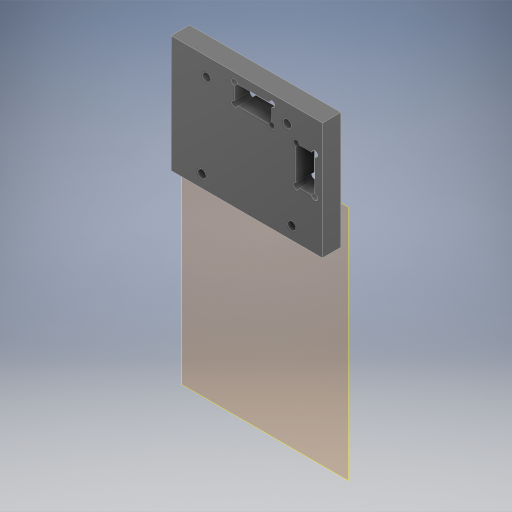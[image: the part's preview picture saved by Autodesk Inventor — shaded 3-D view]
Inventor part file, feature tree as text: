
AUTODESK INVENTOR PART (.ipt)
format: ipt  version: 2024 (Build 280153000, 153)  size: 323,072 bytes
history: native  units: in
note: dims shown in document units (in); Inventor stores cm internally (conversion verified against a paired STEP export)
features: other x3, extrude x3, sketch x3, reference x1
ambient origin geometry x8: Origin, YZ Plane, XZ Plane, XY Plane, X Axis, Y Axis, Z Axis, Center Point
bodies: Body1 (feature_tree)
feature tree (10):
  other  "작업 평면1"
  extrude  "돌출2"  Depth=0.2402in
  extrude  "돌출3"  Depth=0.4764in
  extrude  "돌출4"  Depth=0.2402in
  sketch  "스케치1"
  reference  "참조1"
  sketch  "스케치2"
  sketch  "스케치3"
  other  "조립품16"
  other  "battery_left:1"
